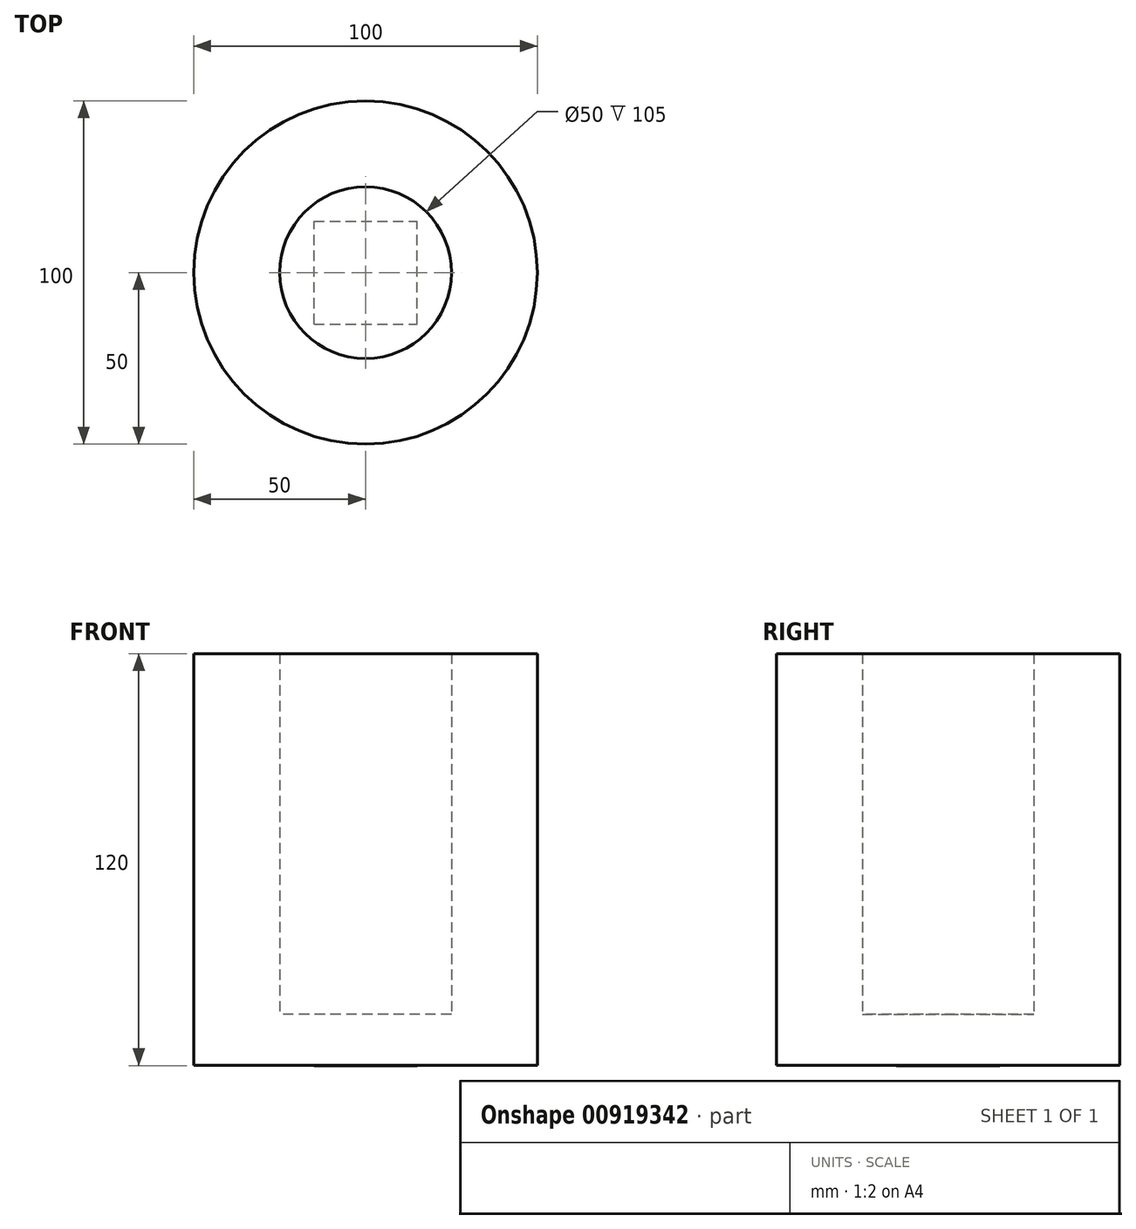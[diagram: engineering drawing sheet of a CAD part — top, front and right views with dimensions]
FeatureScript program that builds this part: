
annotation { "Feature Type Name" : "Feature", "Feature Type Description" : "" }
export const myFeature = defineFeature(function(context is Context, id is Id, definition is map)
    precondition{}
    {
        {
            var Q0;
            Q0=qCreatedBy(makeId("Top.planeOp"),FACE);
            var sketch = newSketch(context, id + "F0", { "sketchPlane" : qUnion([Q0])});
            skCircle(sketch, "E0", {"center": v(0, 0) * mm, "radius": 50 * mm});
            skSolve(sketch);
        }
        {
            var Q0;
            Q0 = qSketchRegion(id + "F0", true);
            extrude(context, id + "F1", {"entities" : qUnion([Q0]), "depth" : 14.9 * mm, "offsetDistance" : 25 * mm});
        }
        {
            var Q0;
            Q0=makeQuery(id+"F1.opExtrude","CAP_FACE",FACE,{"disambiguationData":[OSD([sQuery(id+"F0.wireOp",EDGE,"E0")])],"isStart":false});
            var sketch = newSketch(context, id + "F2", { "sketchPlane" : qUnion([Q0])});
            skCircle(sketch, "E1", {"center": v(0, 0) * mm, "radius": 25 * mm});
            skSolve(sketch);
        }
        {
            var Q0;
            Q0=makeQuery(id+"F2.imprint","IMPRINT",FACE,{"disambiguationData":[TD([[makeQuery(id+"F2.imprint","IMPRINT",EDGE,{"derivedFrom":sQuery(id+"F2.wireOp",EDGE,"E1")}),-1.0]])]});
            extrude(context, id + "F3", {"entities" : qUnion([Q0]), "operationType" : NewBodyOperationType.ADD, "depth" : 105 * mm, "offsetDistance" : 25 * mm});
        }
        {
            var Q0;
            Q0=makeQuery(id+"F1.opExtrude","CAP_FACE",FACE,{"disambiguationData":[OSD([sQuery(id+"F0.wireOp",EDGE,"E0")])],"isStart":true});
            var sketch = newSketch(context, id + "F4", { "sketchPlane" : qUnion([Q0])});
            skLineSegment(sketch, "E2.bottom", {"start": v(-15, 15) * mm, "end": v(15, 15) * mm});
            skLineSegment(sketch, "E2.top", {"start": v(-15, -15) * mm, "end": v(15, -15) * mm});
            skLineSegment(sketch, "E2.left", {"start": v(-15, 15) * mm, "end": v(-15, -15) * mm});
            skLineSegment(sketch, "E2.right", {"start": v(15, 15) * mm, "end": v(15, -15) * mm});
            skSolve(sketch);
        }
        {
            var Q0;
            Q0 = qSketchRegion(id + "F4", true);
            extrude(context, id + "F5", {"entities" : qUnion([Q0]), "operationType" : NewBodyOperationType.ADD, "depth" : 0.1 * mm, "offsetDistance" : 25 * mm});
        }
    });
